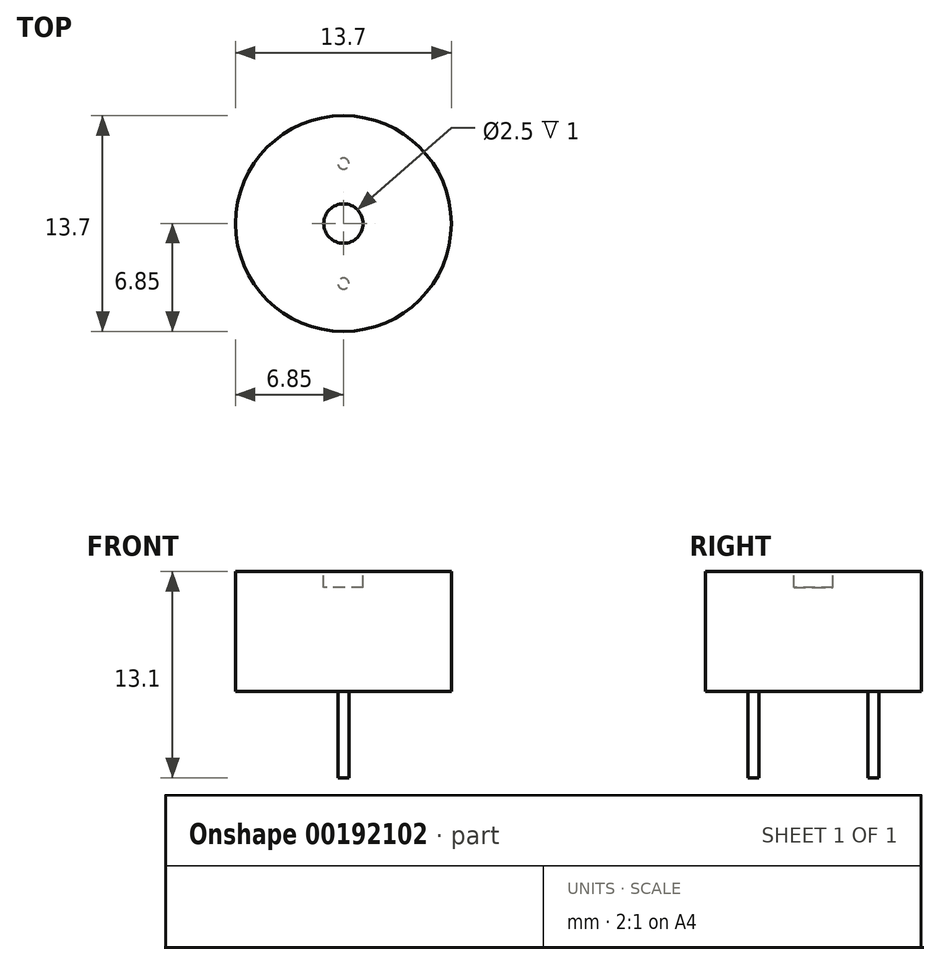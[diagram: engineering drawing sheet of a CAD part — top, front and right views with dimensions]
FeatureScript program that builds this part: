
annotation { "Feature Type Name" : "Feature", "Feature Type Description" : "" }
export const myFeature = defineFeature(function(context is Context, id is Id, definition is map)
    precondition{}
    {
        {
            var Q0;
            Q0=qCreatedBy(makeId("Top.planeOp"),FACE);
            var sketch = newSketch(context, id + "F0", { "sketchPlane" : qUnion([Q0])});
            skCircle(sketch, "E0", {"center": v(0, 0) * mm, "radius": 6.85 * mm});
            skSolve(sketch);
        }
        {
            var Q0;
            Q0 = qSketchRegion(id + "F0", true);
            extrude(context, id + "F1", {"entities" : qUnion([Q0]), "depth" : 7.6 * mm});
        }
        {
            var Q0;
            Q0=makeQuery(id+"F1.opExtrude","CAP_FACE",FACE,{"disambiguationData":[OSD([sQuery(id+"F0.wireOp",EDGE,"E0")])],"isStart":false});
            var sketch = newSketch(context, id + "F2", { "sketchPlane" : qUnion([Q0])});
            skCircle(sketch, "E1", {"center": v(0, 0) * mm, "radius": 1.25 * mm});
            skSolve(sketch);
        }
        {
            var Q0;
            Q0 = qSketchRegion(id + "F2", true);
            extrude(context, id + "F3", {"entities" : qUnion([Q0]), "operationType" : NewBodyOperationType.REMOVE, "oppositeDirection" : true, "depth" : 1 * mm});
        }
        {
            var Q0;
            Q0=makeQuery(id+"F1.opExtrude","CAP_FACE",FACE,{"disambiguationData":[OSD([sQuery(id+"F0.wireOp",EDGE,"E0")])],"isStart":true});
            var sketch = newSketch(context, id + "F4", { "sketchPlane" : qUnion([Q0])});
            skLineSegment(sketch, "E2", {"start": v(0, 6.85) * mm, "end": v(0, -6.85) * mm, "construction": true});
            skCircle(sketch, "E3", {"center": v(0, 3.81) * mm, "radius": 0.35 * mm});
            skCircle(sketch, "E4.MirrorC", {"center": v(0, -3.81) * mm, "radius": 0.35 * mm});
            skSolve(sketch);
        }
        {
            var Q0;
            Q0 = qSketchRegion(id + "F4", true);
            extrude(context, id + "F5", {"entities" : qUnion([Q0]), "operationType" : NewBodyOperationType.ADD, "depth" : 5.5 * mm});
        }
    });
